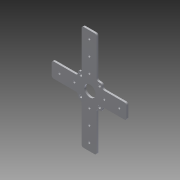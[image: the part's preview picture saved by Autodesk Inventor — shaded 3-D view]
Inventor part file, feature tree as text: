
AUTODESK INVENTOR PART (.ipt)
format: ipt  version: 2014 (Build 180170000, 170)  size: 177,152 bytes
history: native  units: in
note: dims shown in document units (in); Inventor stores cm internally (conversion verified against a paired STEP export)
features: extrude x1, fillet x1, sketch x1
ambient origin geometry x8: Origin, YZ Plane, XZ Plane, XY Plane, X Axis, Y Axis, Z Axis, Center Point
bodies: Solid1 (feature_tree)
feature tree (3):
  extrude  "Extrusion1"  Depth=0.125in
  fillet  "Fillet1"  Radius=1.0in
  sketch  "Sketch1"  dims[d1=0.7874in d3=0.7874in d5=1.1811in d7=0.3937in d9=1.1811in d11=0.3937in d12=1.0in d13=5.0in d14=1.625in d15=0.164in d16=0.164in d17=1.25in d18=1.25in d19=0.1875in d20=0.5in d21=0.5in d22=0.5in d23=0.188in d24=1.25in d25=1.25in d26=0.75in d27=0.8125in d28=2.44in d29=0.5in d30=1.0in d31=2.0in d32=3.0in d33=1.0in d34=3.0in d35=1.625in d36=0.1875in d37=0.8125in d38=0.164in d39=0.164in d40=0.5in d41=0.5in d42=1.0in d43=0.5in d44=0.5in d45=1.0in d46=1.0in d47=1.0in d48=0.125in d49=0.0in d50=0.125in d51=0.7874in d53=1.0in d54=0.3937in d56=1.0in d58=0.7874in d60=1.0in d61=0.3937in d63=1.0in]
